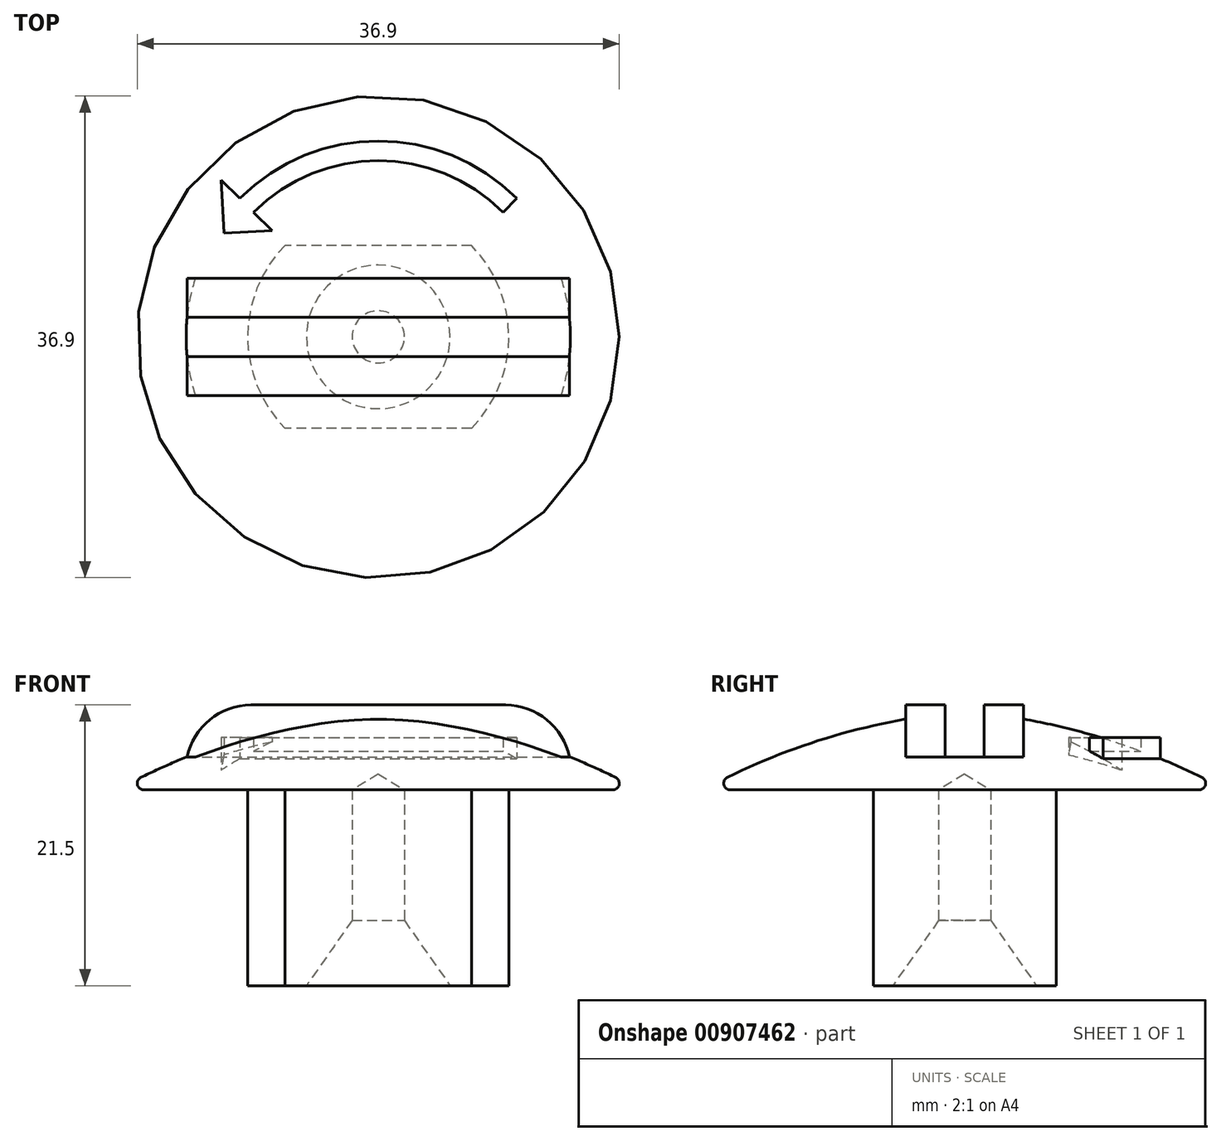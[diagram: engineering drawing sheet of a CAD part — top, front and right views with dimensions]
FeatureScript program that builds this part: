
annotation { "Feature Type Name" : "Feature", "Feature Type Description" : "" }
export const myFeature = defineFeature(function(context is Context, id is Id, definition is map)
    precondition{}
    {
        {
            var Q0;
            Q0=qCreatedBy(makeId("Front.planeOp"),FACE);
            var sketch = newSketch(context, id + "F0", { "sketchPlane" : qUnion([Q0])});
            skArc(sketch, "E0", {"start": v(20, 0) * mm, "mid": v(10.31, 4.04) * mm, "end": v(0, 6) * mm});
            skLineSegment(sketch, "E1", {"start": v(0, 6) * mm, "end": v(0, -15) * mm});
            skLineSegment(sketch, "E2", {"start": v(0, -15) * mm, "end": v(10, -15) * mm});
            skLineSegment(sketch, "E3", {"start": v(10, -15) * mm, "end": v(10, 0) * mm});
            skLineSegment(sketch, "E4", {"start": v(10, 0) * mm, "end": v(20, 0) * mm});
            skSolve(sketch);
        }
        {
            var Q0;
            Q0=makeQuery(id+"F0.imprint","IMPRINT",FACE,{"disambiguationData":[TD([[makeQuery(id+"F0.imprint","IMPRINT",EDGE,{"derivedFrom":sQuery(id+"F0.wireOp",EDGE,"E0")}),1.0]])]});
            var Q1;
            Q1=sQuery(id+"F0.wireOp",EDGE,"E1");
            revolve(context, id + "F1", {"surfaceOperationType" : NewSurfaceOperationType.NEW, "entities" : qUnion([Q0]), "axis" : qUnion([Q1]), "revolveType" : RevolveType.FULL});
        }
        {
            var Q0;
            Q0=qCreatedBy(makeId("Right.planeOp"),FACE);
            var sketch = newSketch(context, id + "F2", { "sketchPlane" : qUnion([Q0])});
            skLineSegment(sketch, "E5.bottom", {"start": v(-1.5, 13.02) * mm, "end": v(1.5, 13.02) * mm});
            skLineSegment(sketch, "E5.top", {"start": v(-1.5, 2.5) * mm, "end": v(1.5, 2.5) * mm});
            skLineSegment(sketch, "E5.left", {"start": v(-1.5, 13.02) * mm, "end": v(-1.5, 2.5) * mm});
            skLineSegment(sketch, "E5.right", {"start": v(1.5, 13.02) * mm, "end": v(1.5, 2.5) * mm});
            skLineSegment(sketch, "E6.bottom", {"start": v(17, -25) * mm, "end": v(7, -25) * mm});
            skLineSegment(sketch, "E6.top", {"start": v(17, 0) * mm, "end": v(7, 0) * mm});
            skLineSegment(sketch, "E6.left", {"start": v(17, -25) * mm, "end": v(17, 0) * mm});
            skLineSegment(sketch, "E6.right", {"start": v(7, -25) * mm, "end": v(7, 0) * mm});
            skLineSegment(sketch, "E7.bottom", {"start": v(-17, -25) * mm, "end": v(-7, -25) * mm});
            skLineSegment(sketch, "E7.top", {"start": v(-17, 0) * mm, "end": v(-7, 0) * mm});
            skLineSegment(sketch, "E7.left", {"start": v(-17, -25) * mm, "end": v(-17, 0) * mm});
            skLineSegment(sketch, "E7.right", {"start": v(-7, -25) * mm, "end": v(-7, 0) * mm});
            skSolve(sketch);
        }
        {
            var Q0;
            Q0=makeQuery(id+"F2.imprint","IMPRINT",FACE,{"disambiguationData":[TD([[makeQuery(id+"F2.imprint","IMPRINT",EDGE,{"derivedFrom":sQuery(id+"F2.wireOp",EDGE,"E5.bottom")}),-1.0]])]});
            var Q1;
            Q1=makeQuery(id+"F2.imprint","IMPRINT",FACE,{"disambiguationData":[TD([[makeQuery(id+"F2.imprint","IMPRINT",EDGE,{"derivedFrom":sQuery(id+"F2.wireOp",EDGE,"E6.bottom")}),-1.0]])]});
            var Q2;
            Q2=makeQuery(id+"F2.imprint","IMPRINT",FACE,{"disambiguationData":[TD([[makeQuery(id+"F2.imprint","IMPRINT",EDGE,{"derivedFrom":sQuery(id+"F2.wireOp",EDGE,"E7.bottom")}),1.0]])]});
            extrude(context, id + "F3", {"entities" : qUnion([Q0, Q1, Q2]), "operationType" : NewBodyOperationType.REMOVE, "oppositeDirection" : true, "depth" : 50 * mm, "offsetDistance" : 25 * mm, "hasSecondDirection" : true, "secondDirectionOppositeDirection" : false, "secondDirectionDepth" : 50 * mm});
        }
        {
            var Q0;
            Q0=makeQuery(id+"F1.opRevolve","SWEPT_FACE",FACE,{"disambiguationData":[OSD([sQuery(id+"F0.wireOp",EDGE,"E2")])]});
            var sketch = newSketch(context, id + "F4", { "sketchPlane" : qUnion([Q0])});
            skCircle(sketch, "E8", {"center": v(0, 0) * mm, "radius": 1.3 * mm});
            skSolve(sketch);
        }
        {
            var Q0;
            Q0=sQuery(id+"F4.wireOp",VERTEX,"E8.center");
            var Q1;
            Q1=makeQuery(id+"F1.opRevolve","SWEPT_BODY",BODY,{"disambiguationData":[OSD([sQuery(id+"F0.wireOp",EDGE,"E0"),sQuery(id+"F0.wireOp",EDGE,"E1"),sQuery(id+"F0.wireOp",EDGE,"E2"),sQuery(id+"F0.wireOp",EDGE,"E3"),sQuery(id+"F0.wireOp",EDGE,"E4")])]});
            hole(context, id + "F5", {"style" : HoleStyle.C_SINK, "endStyle" : HoleEndStyle.BLIND, "holeDiameter" : 4 * mm, "cSinkDiameter" : 11 * mm, "cSinkAngle" : 70 * degree, "majorDiameter" : 5 * mm, "holeDepth" : 15 * mm, "isTappedThrough" : true, "tappedDepth" : 12 * mm, "tapClearance" : 3, "startFromSketch" : true, "locations" : qUnion([Q0]), "scope" : qUnion([Q1])});
        }
        {
            var Q0;
            Q0=makeQuery(id+"F3.boolean.opBoolean","COPY",FACE,{"derivedFrom":makeQuery(id+"F3.opExtrude","SWEPT_FACE",FACE,{"disambiguationData":[OSD([sQuery(id+"F2.wireOp",EDGE,"E5.top")])]})});
            var sketch = newSketch(context, id + "F6", { "sketchPlane" : qUnion([Q0])});
            skLineSegment(sketch, "E9.bottom", {"start": v(-14.64, 1.5) * mm, "end": v(14.64, 1.5) * mm});
            skLineSegment(sketch, "E9.top", {"start": v(-14.64, 4.5) * mm, "end": v(14.64, 4.5) * mm});
            skLineSegment(sketch, "E9.left", {"start": v(-14.64, 1.5) * mm, "end": v(-14.64, 4.5) * mm});
            skLineSegment(sketch, "E9.right", {"start": v(14.64, 1.5) * mm, "end": v(14.64, 4.5) * mm});
            skLineSegment(sketch, "E10.bottom", {"start": v(14.64, -1.5) * mm, "end": v(-14.64, -1.5) * mm});
            skLineSegment(sketch, "E10.top", {"start": v(14.64, -4.5) * mm, "end": v(-14.64, -4.5) * mm});
            skLineSegment(sketch, "E10.left", {"start": v(14.64, -1.5) * mm, "end": v(14.64, -4.5) * mm});
            skLineSegment(sketch, "E10.right", {"start": v(-14.64, -1.5) * mm, "end": v(-14.64, -4.5) * mm});
            skSolve(sketch);
        }
        {
            var Q0;
            Q0=makeQuery(id+"F6.imprint","IMPRINT",FACE,{"disambiguationData":[TD([[makeQuery(id+"F6.imprint","IMPRINT",EDGE,{"derivedFrom":sQuery(id+"F6.wireOp",EDGE,"E10.bottom")}),-1.0]])]});
            var Q1;
            Q1=makeQuery(id+"F6.imprint","IMPRINT",FACE,{"disambiguationData":[TD([[makeQuery(id+"F6.imprint","IMPRINT",EDGE,{"derivedFrom":sQuery(id+"F6.wireOp",EDGE,"E9.bottom")}),1.0]])]});
            extrude(context, id + "F7", {"entities" : qUnion([Q0, Q1]), "operationType" : NewBodyOperationType.ADD, "depth" : 4 * mm, "offsetDistance" : 25 * mm});
        }
        {
            var Q0;
            Q0=makeQuery(id+"F7.opExtrude","CAP_EDGE",EDGE,{"disambiguationData":[OSD([sQuery(id+"F6.wireOp",EDGE,"E10.left")])],"isStart":false});
            var Q1;
            Q1=makeQuery(id+"F7.opExtrude","CAP_EDGE",EDGE,{"disambiguationData":[OSD([sQuery(id+"F6.wireOp",EDGE,"E9.right")])],"isStart":false});
            var Q2;
            Q2=makeQuery(id+"F7.opExtrude","CAP_EDGE",EDGE,{"disambiguationData":[OSD([sQuery(id+"F6.wireOp",EDGE,"E9.left")])],"isStart":false});
            var Q3;
            Q3=makeQuery(id+"F7.opExtrude","CAP_EDGE",EDGE,{"disambiguationData":[OSD([sQuery(id+"F6.wireOp",EDGE,"E10.right")])],"isStart":false});
            fillet(context, id + "F8", {"entities" : qUnion([Q0, Q1, Q2, Q3]), "radius" : 5 * mm, "tangentPropagation" : true, "allowEdgeOverflow" : false});
        }
        {
            var Q0;
            Q0=makeQuery(id+"F3.boolean.opBoolean","INTERSECT",EDGE,{"derivedFrom":[makeQuery(id+"F3.opExtrude","SWEPT_FACE",FACE,{"disambiguationData":[OSD([sQuery(id+"F2.wireOp",EDGE,"E6.top")])]}),makeQuery(id+"F3.opExtrude","SWEPT_FACE",FACE,{"disambiguationData":[OSD([sQuery(id+"F2.wireOp",EDGE,"E7.top")])]})]});
            fillet(context, id + "F9", {"entities" : qUnion([Q0]), "radius" : .5 * mm, "tangentPropagation" : true, "allowEdgeOverflow" : false});
        }
        {
            var Q0;
            Q0=makeQuery(id+"F3.boolean.opBoolean","MERGE",FACE,{"derivedFrom":[makeQuery(id+"F1.opRevolve","SWEPT_FACE",FACE,{"disambiguationData":[OSD([sQuery(id+"F0.wireOp",EDGE,"E4")])]})],"fromTools":[makeQuery(id+"F3.opExtrude","SWEPT_FACE",FACE,{"disambiguationData":[OSD([sQuery(id+"F2.wireOp",EDGE,"E6.top")])]}),makeQuery(id+"F3.opExtrude","SWEPT_FACE",FACE,{"disambiguationData":[OSD([sQuery(id+"F2.wireOp",EDGE,"E7.top")])]})]});
            var sketch = newSketch(context, id + "F10", { "sketchPlane" : qUnion([Q0])});
            skArc(sketch, "E11", {"start": v(-10.6, -10.6) * mm, "mid": v(0, -15) * mm, "end": v(10.6, -10.6) * mm});
            skArc(sketch, "E12", {"start": v(-9.55, -9.55) * mm, "mid": v(0, -13.5) * mm, "end": v(9.55, -9.55) * mm});
            skLineSegment(sketch, "E13", {"start": v(0, 0) * mm, "end": v(-17.68, -17.68) * mm});
            skLineSegment(sketch, "E14", {"start": v(-17.68, -17.68) * mm, "end": v(17.68, -17.68) * mm});
            skLineSegment(sketch, "E15", {"start": v(17.68, -17.68) * mm, "end": v(0, 0) * mm});
            skLineSegment(sketch, "E16", {"start": v(9.55, -9.55) * mm, "end": v(8.13, -8.13) * mm});
            skLineSegment(sketch, "E17", {"start": v(8.13, -8.13) * mm, "end": v(11.82, -7.95) * mm});
            skLineSegment(sketch, "E18", {"start": v(11.82, -7.95) * mm, "end": v(12.02, -12.02) * mm});
            skLineSegment(sketch, "E19", {"start": v(12.02, -12.02) * mm, "end": v(10.6, -10.6) * mm});
            skLineSegment(sketch, "E20.MirrorCS", {"start": v(-8.13, -8.13) * mm, "end": v(-11.82, -7.95) * mm});
            skLineSegment(sketch, "E21.MirrorCS", {"start": v(-11.82, -7.95) * mm, "end": v(-12.02, -12.02) * mm});
            skLineSegment(sketch, "E22.MirrorCS", {"start": v(-17.68, -17.68) * mm, "end": v(0, 0) * mm});
            skSolve(sketch);
        }
        {
            var Q0;
            {var subQ0=sQuery(id+"F10.wireOp",EDGE,"E16");Q0=makeQuery(id+"F10.imprint","IMPRINT",FACE,{"disambiguationData":[TD([[makeQuery(id+"F10.imprint","IMPRINT",EDGE,{"derivedFrom":subQ0}),-1.0]])]});}
            var Q1;
            {var subQ0=sQuery(id+"F10.wireOp",EDGE,"E14");var subQ1=sQuery(id+"F10.wireOp",EDGE,"E11");var subQ2=makeQuery(id+"F10.imprint","INTERSECT",VERTEX,{"disambiguationData":[OD(0.0)],"derivedFrom":[subQ1,subQ0]});Q1=makeQuery(id+"F10.imprint","IMPRINT",FACE,{"disambiguationData":[TD([[makeQuery(id+"F10.imprint","IMPRINT",EDGE,{"disambiguationData":[TD([[subQ2,-1.0]])],"derivedFrom":subQ1}),1.0]])]});}
            var Q2;
            {var subQ0=sQuery(id+"F10.wireOp",EDGE,"E22.MirrorCS");var subQ1=sQuery(id+"F10.wireOp",EDGE,"E11");var subQ2=makeQuery(id+"F10.imprint","INTERSECT",VERTEX,{"derivedFrom":[subQ1,subQ0]});Q2=makeQuery(id+"F10.imprint","IMPRINT",FACE,{"disambiguationData":[TD([[makeQuery(id+"F10.imprint","IMPRINT",EDGE,{"disambiguationData":[TD([[subQ2,-1.0]])],"derivedFrom":subQ1}),1.0]])]});}
            var Q3;
            {var subQ4=sQuery(id+"F10.wireOp",EDGE,"E20.MirrorCS");Q3=makeQuery(id+"F10.imprint","IMPRINT",FACE,{"disambiguationData":[TD([[makeQuery(id+"F10.imprint","IMPRINT",EDGE,{"derivedFrom":subQ4}),1.0]])]});}
            extrude(context, id + "F11", {"entities" : qUnion([Q0, Q1, Q2, Q3]), "operationType" : NewBodyOperationType.ADD, "oppositeDirection" : true, "depth" : 4 * mm, "offsetDistance" : 25 * mm});
        }
    });
